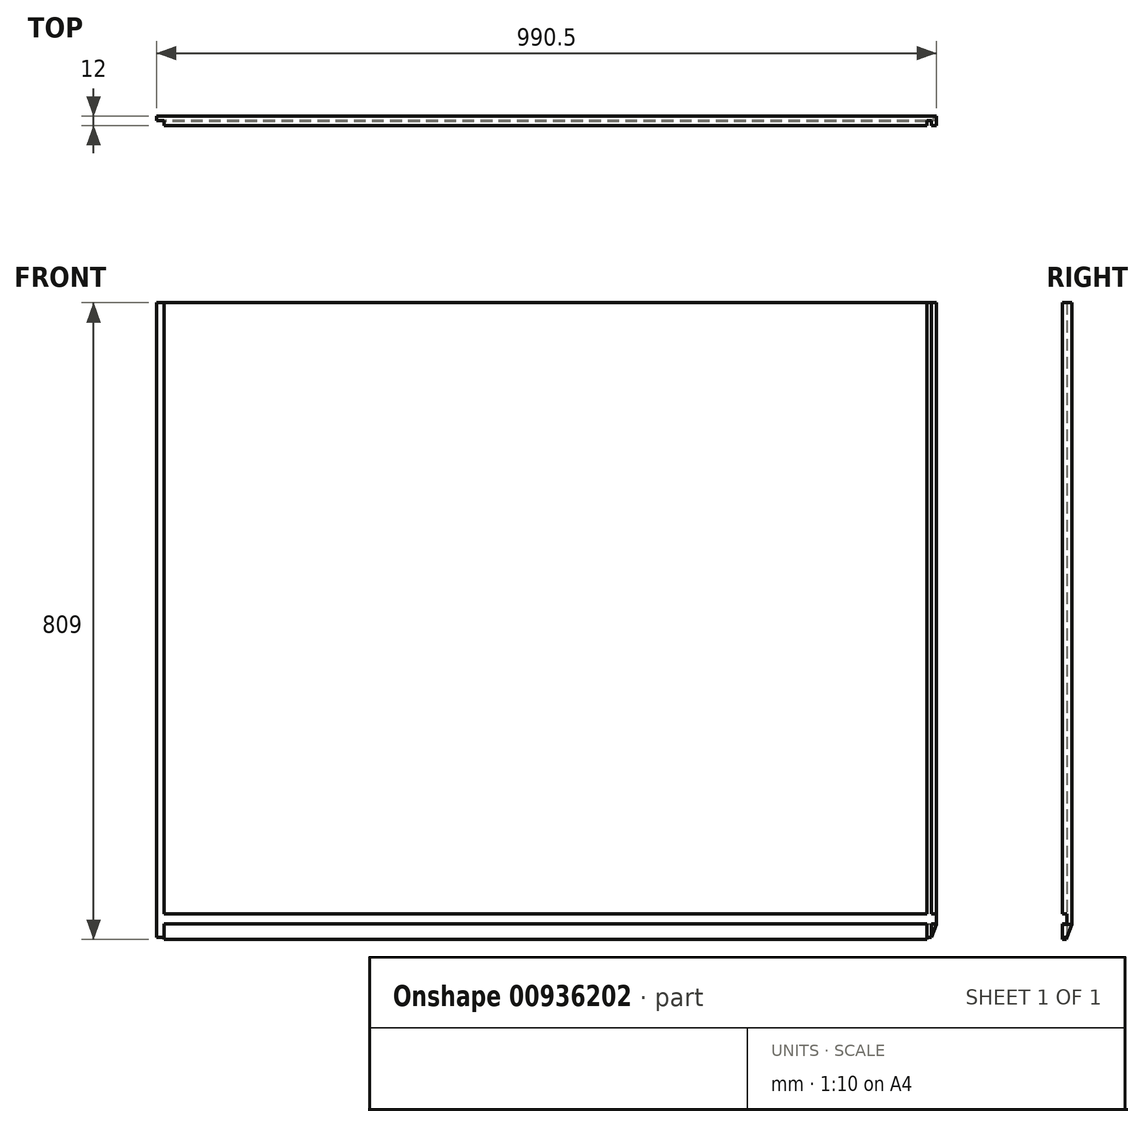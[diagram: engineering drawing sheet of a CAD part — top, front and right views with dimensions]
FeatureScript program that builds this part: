
annotation { "Feature Type Name" : "Feature", "Feature Type Description" : "" }
export const myFeature = defineFeature(function(context is Context, id is Id, definition is map)
    precondition{}
    {
        {
            var Q0;
            Q0=qCreatedBy(makeId("Top.planeOp"),FACE);
            var sketch = newSketch(context, id + "F0", { "sketchPlane" : qUnion([Q0])});
            skLineSegment(sketch, "E0.bottom", {"start": v(0, 0) * mm, "end": v(990.5, 0) * mm});
            skLineSegment(sketch, "E0.top", {"start": v(0, -12) * mm, "end": v(990.5, -12) * mm});
            skLineSegment(sketch, "E0.left", {"start": v(0, 0) * mm, "end": v(0, -12) * mm});
            skLineSegment(sketch, "E0.right", {"start": v(990.5, 0) * mm, "end": v(990.5, -12) * mm});
            skSolve(sketch);
        }
        {
            var Q0;
            Q0 = qSketchRegion(id + "F0", true);
            extrude(context, id + "F1", {"entities" : qUnion([Q0]), "depth" : 899 * mm, "offsetDistance" : 25 * mm});
        }
        {
            var Q0;
            Q0=qCreatedBy(makeId("Top.planeOp"),FACE);
            var sketch = newSketch(context, id + "F2", { "sketchPlane" : qUnion([Q0])});
            skLineSegment(sketch, "E1.bottom", {"start": v(0, -6) * mm, "end": v(9.5, -6) * mm});
            skLineSegment(sketch, "E1.top", {"start": v(0, -12) * mm, "end": v(9.5, -12) * mm});
            skLineSegment(sketch, "E1.left", {"start": v(0, -6) * mm, "end": v(0, -12) * mm});
            skLineSegment(sketch, "E1.right", {"start": v(9.5, -6) * mm, "end": v(9.5, -12) * mm});
            skSolve(sketch);
        }
        {
            var Q0;
            Q0 = qSketchRegion(id + "F2", true);
            extrude(context, id + "F3", {"entities" : qUnion([Q0]), "operationType" : NewBodyOperationType.REMOVE, "endBound" : BoundingType.THROUGH_ALL, "depth" : 25 * mm, "offsetDistance" : 25 * mm});
        }
        {
            var Q0;
            Q0=qCreatedBy(makeId("Top.planeOp"),FACE);
            var sketch = newSketch(context, id + "F4", { "sketchPlane" : qUnion([Q0])});
            skLineSegment(sketch, "E2.bottom", {"start": v(984.5, -12) * mm, "end": v(978.5, -12) * mm});
            skLineSegment(sketch, "E2.top", {"start": v(984.5, -6) * mm, "end": v(978.5, -6) * mm});
            skLineSegment(sketch, "E2.left", {"start": v(984.5, -12) * mm, "end": v(984.5, -6) * mm});
            skLineSegment(sketch, "E2.right", {"start": v(978.5, -12) * mm, "end": v(978.5, -6) * mm});
            skSolve(sketch);
        }
        {
            var Q0;
            Q0 = qSketchRegion(id + "F4", true);
            extrude(context, id + "F5", {"entities" : qUnion([Q0]), "operationType" : NewBodyOperationType.REMOVE, "endBound" : BoundingType.THROUGH_ALL, "depth" : 25 * mm, "offsetDistance" : 25 * mm});
        }
        {
            var Q0;
            Q0=qCreatedBy(makeId("Right.planeOp"),FACE);
            var sketch = newSketch(context, id + "F6", { "sketchPlane" : qUnion([Q0])});
            skLineSegment(sketch, "E3.bottom", {"start": v(-12, 122.5) * mm, "end": v(-6, 122.5) * mm});
            skLineSegment(sketch, "E3.top", {"start": v(-12, 110) * mm, "end": v(-6, 110) * mm});
            skLineSegment(sketch, "E3.left", {"start": v(-12, 122.5) * mm, "end": v(-12, 110) * mm});
            skLineSegment(sketch, "E3.right", {"start": v(-6, 122.5) * mm, "end": v(-6, 110) * mm});
            skSolve(sketch);
        }
        {
            var Q0;
            Q0 = qSketchRegion(id + "F6", true);
            extrude(context, id + "F7", {"entities" : qUnion([Q0]), "operationType" : NewBodyOperationType.REMOVE, "endBound" : BoundingType.THROUGH_ALL, "depth" : 25 * mm, "offsetDistance" : 25 * mm});
        }
        {
            var Q0;
            Q0=qCreatedBy(makeId("Right.planeOp"),FACE);
            var sketch = newSketch(context, id + "F8", { "sketchPlane" : qUnion([Q0])});
            skLineSegment(sketch, "E4.bottom", {"start": v(0, 0) * mm, "end": v(-25, 0) * mm});
            skLineSegment(sketch, "E4.top", {"start": v(-6.92, 90) * mm, "end": v(-25, 90) * mm});
            skLineSegment(sketch, "E4.left", {"start": v(0, 0) * mm, "end": v(0, 109) * mm});
            skLineSegment(sketch, "E4.right", {"start": v(-25, 0) * mm, "end": v(-25, 90) * mm});
            skLineSegment(sketch, "E5", {"start": v(0, 109) * mm, "end": v(-6.92, 90) * mm});
            skPoint(sketch, "E6.orphan", {"position": v(0, 90) * mm});
            skSolve(sketch);
        }
        {
            var Q0;
            Q0 = qSketchRegion(id + "F8", true);
            extrude(context, id + "F9", {"entities" : qUnion([Q0]), "operationType" : NewBodyOperationType.REMOVE, "endBound" : BoundingType.THROUGH_ALL, "depth" : 25 * mm, "offsetDistance" : 25 * mm});
        }
        {
            var Q0;
            {var subQ0=sQuery(id+"F0.wireOp",EDGE,"E0.right");var subQ2=sQuery(id+"F0.wireOp",EDGE,"E0.top");var subQ5=makeQuery(id+"F1.opExtrude","SWEPT_FACE",FACE,{"disambiguationData":[OSD([subQ0])]});Q0=makeQuery(id+"F7.boolean.opBoolean","SPLIT",FACE,{"disambiguationData":[TD([makeQuery(id+"F7.opExtrude","SWEPT_FACE",FACE,{"disambiguationData":[OSD([sQuery(id+"F6.wireOp",EDGE,"E3.top")])]})])],"derivedFrom":makeQuery(id+"F5.boolean.opBoolean","SPLIT",FACE,{"disambiguationData":[TD([subQ5])],"derivedFrom":makeQuery(id+"F1.opExtrude","SWEPT_FACE",FACE,{"disambiguationData":[OSD([subQ2])]})})});}
            var sketch = newSketch(context, id + "F10", { "sketchPlane" : qUnion([Q0])});
            skLineSegment(sketch, "E7.0", {"start": v(990.5, 90) * mm, "end": v(990.5, 109) * mm});
            skLineSegment(sketch, "E8", {"start": v(990.5, 109) * mm, "end": v(983.58, 90) * mm});
            skLineSegment(sketch, "E9", {"start": v(983.58, 90) * mm, "end": v(990.5, 90) * mm});
            skSolve(sketch);
        }
        {
            var Q0;
            Q0 = qSketchRegion(id + "F10", true);
            extrude(context, id + "F11", {"entities" : qUnion([Q0]), "operationType" : NewBodyOperationType.REMOVE, "endBound" : BoundingType.THROUGH_ALL, "oppositeDirection" : true, "depth" : 25 * mm, "offsetDistance" : 25 * mm});
        }
    });
